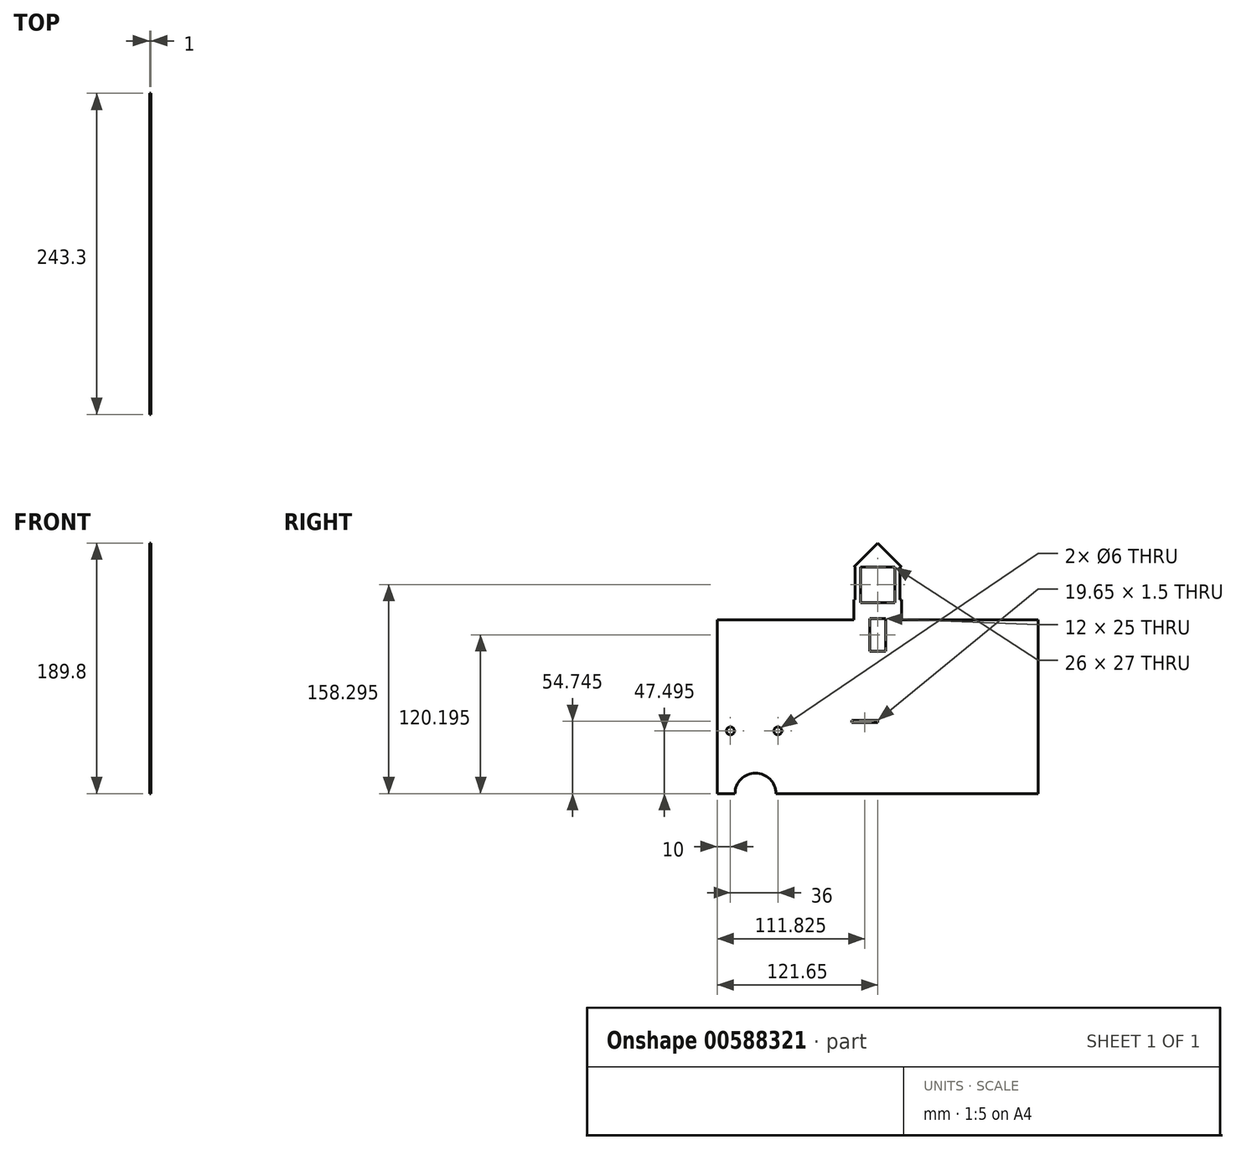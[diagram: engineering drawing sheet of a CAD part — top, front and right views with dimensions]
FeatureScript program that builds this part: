
annotation { "Feature Type Name" : "Feature", "Feature Type Description" : "" }
export const myFeature = defineFeature(function(context is Context, id is Id, definition is map)
    precondition{}
    {
        {
            var Q0;
            Q0=qCreatedBy(makeId("Right.planeOp"),FACE);
            var sketch = newSketch(context, id + "F0", { "sketchPlane" : qUnion([Q0])});
            skLineSegment(sketch, "E0.bottom", {"start": v(19.65, -16.37) * mm, "end": v(-19.65, -16.38) * mm});
            skLineSegment(sketch, "E0.top", {"start": v(19.65, 16.38) * mm, "end": v(-19.65, 16.37) * mm});
            skLineSegment(sketch, "E0.left", {"start": v(19.65, -16.37) * mm, "end": v(19.65, 16.38) * mm});
            skLineSegment(sketch, "E0.right", {"start": v(-19.65, -16.38) * mm, "end": v(-19.65, 16.37) * mm});
            skPoint(sketch, "E0.middle", {"position": v(0, 0) * mm});
            skLineSegment(sketch, "E1", {"start": v(123.65, 16.38) * mm, "end": v(19.65, 16.38) * mm});
            skLineSegment(sketch, "E2", {"start": v(19.65, -16.37) * mm, "end": v(123.65, -16.38) * mm});
            skLineSegment(sketch, "E3", {"start": v(-19.65, -16.38) * mm, "end": v(-123.65, -16.38) * mm});
            skLineSegment(sketch, "E4", {"start": v(-123.65, 16.37) * mm, "end": v(-47.65, 16.37) * mm});
            skLineSegment(sketch, "E5", {"start": v(123.65, 89.38) * mm, "end": v(121.65, 89.38) * mm});
            skLineSegment(sketch, "E6", {"start": v(-19.65, 16.37) * mm, "end": v(-36.65, 16.37) * mm});
            skLineSegment(sketch, "E7", {"start": v(-36.65, 15.38) * mm, "end": v(-36.65, 5.37) * mm});
            skLineSegment(sketch, "E8", {"start": v(-47.65, 5.37) * mm, "end": v(-47.65, 15.38) * mm});
            skLineSegment(sketch, "E9", {"start": v(-47.65, 16.37) * mm, "end": v(-61.65, 16.37) * mm});
            skLineSegment(sketch, "E10", {"start": v(-61.65, 16.37) * mm, "end": v(-61.65, -16.38) * mm});
            skLineSegment(sketch, "E11", {"start": v(0, 0) * mm, "end": v(0, 16.38) * mm});
            skLineSegment(sketch, "E12", {"start": v(0, 16.38) * mm, "end": v(0, 29.48) * mm});
            skLineSegment(sketch, "E13", {"start": v(0, 29.48) * mm, "end": v(6, 29.48) * mm});
            skLineSegment(sketch, "E14", {"start": v(6, 29.48) * mm, "end": v(6, 57.48) * mm});
            skLineSegment(sketch, "E15", {"start": v(-6, 57.48) * mm, "end": v(-6, 29.47) * mm});
            skLineSegment(sketch, "E16", {"start": v(-6, 29.48) * mm, "end": v(0, 29.48) * mm});
            skLineSegment(sketch, "E17", {"start": v(-19.65, 16.37) * mm, "end": v(-19.65, 14.87) * mm});
            skLineSegment(sketch, "E18", {"start": v(-19.65, 14.87) * mm, "end": v(19.65, 14.87) * mm});
            skLineSegment(sketch, "E19", {"start": v(-123.65, -39.13) * mm, "end": v(-92.65, -39.13) * mm});
            skLineSegment(sketch, "E20", {"start": v(-61.65, -39.13) * mm, "end": v(-61.65, -16.38) * mm});
            skLineSegment(sketch, "E21", {"start": v(-123.65, -39.13) * mm, "end": v(-108.15, -39.13) * mm});
            skArc(sketch, "E22", {"start": v(-73.65, -39.13) * mm, "mid": v(-92.65, -20.13) * mm, "end": v(-111.65, -39.13) * mm});
            skLineSegment(sketch, "E23", {"start": v(-61.65, 16.37) * mm, "end": v(-75.65, 16.37) * mm});
            skLineSegment(sketch, "E24", {"start": v(-75.65, 16.37) * mm, "end": v(-75.65, 8.37) * mm});
            skLineSegment(sketch, "E25", {"start": v(-123.65, 16.37) * mm, "end": v(-111.65, 16.37) * mm});
            skLineSegment(sketch, "E26", {"start": v(-111.65, 16.37) * mm, "end": v(-111.65, 8.37) * mm});
            skCircle(sketch, "E27", {"center": v(-111.65, 8.37) * mm, "radius": 3 * mm});
            skCircle(sketch, "E28", {"center": v(-75.65, 8.37) * mm, "radius": 3 * mm});
            skLineSegment(sketch, "E29", {"start": v(-6, 57.48) * mm, "end": v(-28, 57.48) * mm});
            skLineSegment(sketch, "E30", {"start": v(-28, 57.48) * mm, "end": v(-28, 41.98) * mm});
            skLineSegment(sketch, "E31", {"start": v(-28, 57.48) * mm, "end": v(-47, 57.48) * mm});
            skLineSegment(sketch, "E32", {"start": v(-47, 41.98) * mm, "end": v(-47, 57.48) * mm});
            skLineSegment(sketch, "E33", {"start": v(6, 57.48) * mm, "end": v(6, 70.58) * mm});
            skLineSegment(sketch, "E34", {"start": v(-6, 70.58) * mm, "end": v(-6, 92.57) * mm});
            skLineSegment(sketch, "E35", {"start": v(6, 92.57) * mm, "end": v(6, 70.58) * mm});
            skLineSegment(sketch, "E36", {"start": v(0, 92.57) * mm, "end": v(0, 105.67) * mm});
            skLineSegment(sketch, "E37", {"start": v(0, 105.67) * mm, "end": v(13, 105.67) * mm});
            skLineSegment(sketch, "E38", {"start": v(0, 105.67) * mm, "end": v(-13, 105.67) * mm});
            skLineSegment(sketch, "E39", {"start": v(-18, 105.67) * mm, "end": v(-18, 107.67) * mm});
            skLineSegment(sketch, "E40", {"start": v(18, 105.67) * mm, "end": v(18, 107.67) * mm});
            skLineSegment(sketch, "E41", {"start": v(0, 150.68) * mm, "end": v(-18, 132.67) * mm});
            skLineSegment(sketch, "E42", {"start": v(0, 150.68) * mm, "end": v(18, 132.67) * mm});
            skLineSegment(sketch, "E43", {"start": v(18, 92.57) * mm, "end": v(123.65, 92.57) * mm});
            skLineSegment(sketch, "E44", {"start": v(-18, 92.57) * mm, "end": v(-123.65, 92.57) * mm});
            skLineSegment(sketch, "E45", {"start": v(-123.65, 89.38) * mm, "end": v(-123.65, 92.57) * mm});
            skLineSegment(sketch, "E46", {"start": v(18, 105.67) * mm, "end": v(18, 92.57) * mm});
            skLineSegment(sketch, "E47", {"start": v(-18, 105.67) * mm, "end": v(-18, 92.57) * mm});
            skLineSegment(sketch, "E48", {"start": v(-97.65, 89.38) * mm, "end": v(-97.65, 85.38) * mm});
            skLineSegment(sketch, "E49", {"start": v(-97.65, 85.38) * mm, "end": v(-86.65, 85.38) * mm});
            skLineSegment(sketch, "E50", {"start": v(-86.65, 85.38) * mm, "end": v(-86.65, 73.38) * mm});
            skLineSegment(sketch, "E51", {"start": v(-97.65, 73.38) * mm, "end": v(-97.65, 85.38) * mm});
            skLineSegment(sketch, "E52", {"start": v(-18, 132.67) * mm, "end": v(-17, 132.67) * mm});
            skLineSegment(sketch, "E53", {"start": v(-13, 132.67) * mm, "end": v(-13, 105.67) * mm});
            skLineSegment(sketch, "E54", {"start": v(18, 132.67) * mm, "end": v(17, 132.67) * mm});
            skLineSegment(sketch, "E55", {"start": v(13, 132.67) * mm, "end": v(13, 105.67) * mm});
            skLineSegment(sketch, "E56", {"start": v(-13, 132.67) * mm, "end": v(13, 132.67) * mm});
            skLineSegment(sketch, "E57", {"start": v(0, 150.68) * mm, "end": v(0, 105.67) * mm});
            skLineSegment(sketch, "E58", {"start": v(6, 92.57) * mm, "end": v(6, 89.38) * mm});
            skLineSegment(sketch, "E59", {"start": v(56, 89.38) * mm, "end": v(56, 79.38) * mm});
            skLineSegment(sketch, "E60", {"start": v(70, 79.38) * mm, "end": v(70, 89.38) * mm});
            skLineSegment(sketch, "E61", {"start": v(70, 89.38) * mm, "end": v(56, 89.38) * mm});
            skLineSegment(sketch, "E62", {"start": v(6, 57.48) * mm, "end": v(33, 57.48) * mm});
            skLineSegment(sketch, "E63", {"start": v(33, 57.48) * mm, "end": v(33, 53.47) * mm});
            skLineSegment(sketch, "E64", {"start": v(33, 53.47) * mm, "end": v(46, 53.47) * mm});
            skLineSegment(sketch, "E65", {"start": v(46, 53.47) * mm, "end": v(46, 43.47) * mm});
            skLineSegment(sketch, "E66", {"start": v(33, 43.47) * mm, "end": v(33, 53.47) * mm});
            skLineSegment(sketch, "E67", {"start": v(46, 43.47) * mm, "end": v(80, 43.47) * mm});
            skLineSegment(sketch, "E68", {"start": v(80, 43.47) * mm, "end": v(80, 41.98) * mm});
            skLineSegment(sketch, "E69", {"start": v(89, 41.98) * mm, "end": v(89, 53.48) * mm});
            skLineSegment(sketch, "E70", {"start": v(80, 53.48) * mm, "end": v(80, 43.47) * mm});
            skLineSegment(sketch, "E71", {"start": v(46, 43.47) * mm, "end": v(47.5, 43.47) * mm});
            skLineSegment(sketch, "E72", {"start": v(-19.65, 16.38) * mm, "end": v(-19.65, 92.57) * mm});
            skLineSegment(sketch, "E73", {"start": v(19.65, 16.38) * mm, "end": v(19.65, 92.57) * mm});
            skLineSegment(sketch, "E74", {"start": v(89, 53.48) * mm, "end": v(89, 53.98) * mm});
            skLineSegment(sketch, "E75", {"start": v(89, 53.98) * mm, "end": v(79.57, 53.98) * mm});
            skLineSegment(sketch, "E76", {"start": v(80, 53.48) * mm, "end": v(80, 53.98) * mm});
            skLineSegment(sketch, "E77", {"start": v(-47.65, 15.38) * mm, "end": v(-36.65, 15.38) * mm});
            skLineSegment(sketch, "E78.trimOffspring", {"start": v(-36.65, 16.37) * mm, "end": v(-19.65, 16.37) * mm});
            skLineSegment(sketch, "E79", {"start": v(6, 70.58) * mm, "end": v(6, 68.58) * mm});
            skLineSegment(sketch, "E80", {"start": v(6, 68.58) * mm, "end": v(-6, 68.58) * mm});
            skLineSegment(sketch, "E81", {"start": v(-6, 68.58) * mm, "end": v(-6, 70.58) * mm});
            skArc(sketch, "E82", {"start": v(-77.15, -39.13) * mm, "mid": v(-92.65, -23.63) * mm, "end": v(-108.15, -39.13) * mm});
            skLineSegment(sketch, "E83", {"start": v(123.65, 92.57) * mm, "end": v(121.65, 92.57) * mm});
            skLineSegment(sketch, "E84", {"start": v(121.65, 92.57) * mm, "end": v(121.65, -16.38) * mm});
            skLineSegment(sketch, "E85", {"start": v(121.65, -16.38) * mm, "end": v(121.65, -39.13) * mm});
            skLineSegment(sketch, "E86", {"start": v(121.65, -39.13) * mm, "end": v(-61.65, -39.13) * mm});
            skLineSegment(sketch, "E87", {"start": v(-123.65, 92.57) * mm, "end": v(-121.65, 92.57) * mm});
            skLineSegment(sketch, "E88", {"start": v(-121.65, 92.57) * mm, "end": v(-121.65, -39.12) * mm});
            skPoint(sketch, "E88.endSnap0", {"position": v(-115.9, -39.13) * mm});
            skLineSegment(sketch, "E89.trimOffspring", {"start": v(-77.15, -39.13) * mm, "end": v(-61.65, -39.13) * mm});
            skLineSegment(sketch, "E90.trimOffspring", {"start": v(-97.65, 89.38) * mm, "end": v(-121.65, 89.38) * mm});
            skLineSegment(sketch, "E91", {"start": v(-6, 92.57) * mm, "end": v(-6, 93.58) * mm});
            skLineSegment(sketch, "E92", {"start": v(-6, 93.57) * mm, "end": v(6, 93.57) * mm});
            skLineSegment(sketch, "E93", {"start": v(6, 93.57) * mm, "end": v(6, 92.57) * mm});
            skLineSegment(sketch, "E94", {"start": v(-18, 107.67) * mm, "end": v(-17, 107.67) * mm});
            skLineSegment(sketch, "E95", {"start": v(-17, 107.67) * mm, "end": v(-17, 132.67) * mm});
            skLineSegment(sketch, "E96", {"start": v(18, 107.67) * mm, "end": v(17, 107.67) * mm});
            skLineSegment(sketch, "E97", {"start": v(17, 107.67) * mm, "end": v(17, 132.67) * mm});
            skSolve(sketch);
        }
        {
            var Q0;
            {var subQ3=sQuery(id+"F0.wireOp",EDGE,"E84");var subQ10=makeQuery(id+"F0.imprint","IMPRINT",VERTEX,{"derivedFrom":subQ3});Q0=makeQuery(id+"F0.imprint","IMPRINT",FACE,{"disambiguationData":[TD([[makeQuery(id+"F0.imprint","IMPRINT",EDGE,{"disambiguationData":[TD([[subQ10,1.0]])],"derivedFrom":subQ3}),-1.0]])]});}
            var Q1;
            {var subQ1=sQuery(id+"F0.wireOp",EDGE,"E0.left");var subQ8=makeQuery(id+"F0.imprint","INTERSECT",VERTEX,{"derivedFrom":[subQ1,sQuery(id+"F0.wireOp",EDGE,"E18")]});Q1=makeQuery(id+"F0.imprint","IMPRINT",FACE,{"disambiguationData":[TD([[makeQuery(id+"F0.imprint","IMPRINT",EDGE,{"disambiguationData":[TD([[subQ8,1.0]])],"derivedFrom":subQ1}),-1.0]])]});}
            var Q2;
            {var subQ3=sQuery(id+"F0.wireOp",EDGE,"E0.bottom");Q2=makeQuery(id+"F0.imprint","IMPRINT",FACE,{"disambiguationData":[TD([[makeQuery(id+"F0.imprint","IMPRINT",EDGE,{"derivedFrom":subQ3}),1.0]])]});}
            var Q3;
            {var subQ4=sQuery(id+"F0.wireOp",EDGE,"E0.bottom");Q3=makeQuery(id+"F0.imprint","IMPRINT",FACE,{"disambiguationData":[TD([[makeQuery(id+"F0.imprint","IMPRINT",EDGE,{"derivedFrom":subQ4}),-1.0]])]});}
            var Q4;
            {var subQ11=sQuery(id+"F0.wireOp",EDGE,"E0.right");Q4=makeQuery(id+"F0.imprint","IMPRINT",FACE,{"disambiguationData":[TD([[makeQuery(id+"F0.imprint","IMPRINT",EDGE,{"derivedFrom":subQ11}),1.0]])]});}
            var Q5;
            {var subQ6=sQuery(id+"F0.wireOp",EDGE,"E4");Q5=makeQuery(id+"F0.imprint","IMPRINT",FACE,{"disambiguationData":[TD([[makeQuery(id+"F0.imprint","IMPRINT",EDGE,{"derivedFrom":subQ6}),-1.0]])]});}
            var Q6;
            {var subQ4=sQuery(id+"F0.wireOp",EDGE,"E20");Q6=makeQuery(id+"F0.imprint","IMPRINT",FACE,{"disambiguationData":[TD([[makeQuery(id+"F0.imprint","IMPRINT",EDGE,{"derivedFrom":subQ4}),1.0]])]});}
            var Q7;
            {var subQ2=sQuery(id+"F0.wireOp",EDGE,"E22");Q7=makeQuery(id+"F0.imprint","IMPRINT",FACE,{"disambiguationData":[TD([[makeQuery(id+"F0.imprint","IMPRINT",EDGE,{"derivedFrom":subQ2}),1.0]])]});}
            var Q8;
            {var subQ0=sQuery(id+"F0.wireOp",EDGE,"E0.left");var subQ5=sQuery(id+"F0.wireOp",EDGE,"E18");var subQ6=makeQuery(id+"F0.imprint","INTERSECT",VERTEX,{"derivedFrom":[subQ0,subQ5]});Q8=makeQuery(id+"F0.imprint","IMPRINT",FACE,{"disambiguationData":[TD([[makeQuery(id+"F0.imprint","IMPRINT",EDGE,{"disambiguationData":[TD([[subQ6,1.0]])],"derivedFrom":subQ5}),1.0]])]});}
            var Q9;
            {var subQ1=sQuery(id+"F0.wireOp",EDGE,"E12");Q9=makeQuery(id+"F0.imprint","IMPRINT",FACE,{"disambiguationData":[TD([[makeQuery(id+"F0.imprint","IMPRINT",EDGE,{"derivedFrom":subQ1}),-1.0]])]});}
            var Q10;
            {var subQ1=sQuery(id+"F0.wireOp",EDGE,"E12");Q10=makeQuery(id+"F0.imprint","IMPRINT",FACE,{"disambiguationData":[TD([[makeQuery(id+"F0.imprint","IMPRINT",EDGE,{"derivedFrom":subQ1}),1.0]])]});}
            var Q11;
            {var subQ0=sQuery(id+"F0.wireOp",EDGE,"E17");Q11=makeQuery(id+"F0.imprint","IMPRINT",FACE,{"disambiguationData":[TD([[makeQuery(id+"F0.imprint","IMPRINT",EDGE,{"derivedFrom":subQ0}),1.0]])]});}
            var Q12;
            {var subQ6=sQuery(id+"F0.wireOp",EDGE,"E33");Q12=makeQuery(id+"F0.imprint","IMPRINT",FACE,{"disambiguationData":[TD([[makeQuery(id+"F0.imprint","IMPRINT",EDGE,{"derivedFrom":subQ6}),-1.0]])]});}
            var Q13;
            Q13=makeQuery(id+"F0.imprint","IMPRINT",FACE,{"disambiguationData":[TD([[makeQuery(id+"F0.imprint","IMPRINT",EDGE,{"derivedFrom":sQuery(id+"F0.wireOp",EDGE,"E13")}),1.0]])]});
            var Q14;
            {var subQ6=sQuery(id+"F0.wireOp",EDGE,"E58");Q14=makeQuery(id+"F0.imprint","IMPRINT",FACE,{"disambiguationData":[TD([[makeQuery(id+"F0.imprint","IMPRINT",EDGE,{"derivedFrom":subQ6}),1.0]])]});}
            var Q15;
            {var subQ4=sQuery(id+"F0.wireOp",EDGE,"if9FEv0G-EfnI-fkLM-PL1J-uSAs0mxL8H2t");Q15=makeQuery(id+"F0.imprint","IMPRINT",FACE,{"disambiguationData":[TD([[makeQuery(id+"F0.imprint","IMPRINT",EDGE,{"derivedFrom":subQ4}),-1.0]])]});}
            var Q16;
            {var subQ4=sQuery(id+"F0.wireOp",EDGE,"OIBqOK52-HsA3-W79x-OM3V-7rghKtutOd8c");Q16=makeQuery(id+"F0.imprint","IMPRINT",FACE,{"disambiguationData":[TD([[makeQuery(id+"F0.imprint","IMPRINT",EDGE,{"derivedFrom":subQ4}),1.0]])]});}
            var Q17;
            {var subQ1=sQuery(id+"F0.wireOp",EDGE,"E44");var subQ8=makeQuery(id+"F0.imprint","INTERSECT",VERTEX,{"derivedFrom":[subQ1,sQuery(id+"F0.wireOp",EDGE,"E47")]});Q17=makeQuery(id+"F0.imprint","IMPRINT",FACE,{"disambiguationData":[TD([[makeQuery(id+"F0.imprint","IMPRINT",EDGE,{"disambiguationData":[TD([[subQ8,-1.0]])],"derivedFrom":subQ1}),1.0]])]});}
            var Q18;
            {var subQ0=sQuery(id+"F0.wireOp",EDGE,"E40");Q18=makeQuery(id+"F0.imprint","IMPRINT",FACE,{"disambiguationData":[TD([[makeQuery(id+"F0.imprint","IMPRINT",EDGE,{"derivedFrom":subQ0}),1.0]])]});}
            var Q19;
            {var subQ0=sQuery(id+"F0.wireOp",EDGE,"E39");Q19=makeQuery(id+"F0.imprint","IMPRINT",FACE,{"disambiguationData":[TD([[makeQuery(id+"F0.imprint","IMPRINT",EDGE,{"derivedFrom":subQ0}),-1.0]])]});}
            var Q20;
            {var subQ0=sQuery(id+"F0.wireOp",EDGE,"E41");Q20=makeQuery(id+"F0.imprint","IMPRINT",FACE,{"disambiguationData":[TD([[makeQuery(id+"F0.imprint","IMPRINT",EDGE,{"derivedFrom":subQ0}),1.0]])]});}
            var Q21;
            {var subQ0=sQuery(id+"F0.wireOp",EDGE,"E42");Q21=makeQuery(id+"F0.imprint","IMPRINT",FACE,{"disambiguationData":[TD([[makeQuery(id+"F0.imprint","IMPRINT",EDGE,{"derivedFrom":subQ0}),-1.0]])]});}
            extrude(context, id + "F1", {"entities" : qUnion([Q0, Q1, Q2, Q3, Q4, Q5, Q6, Q7, Q8, Q9, Q10, Q11, Q12, Q13, Q14, Q15, Q16, Q17, Q18, Q19, Q20, Q21]), "depth" : 1 * mm, "offsetDistance" : 25 * mm});
        }
    });
